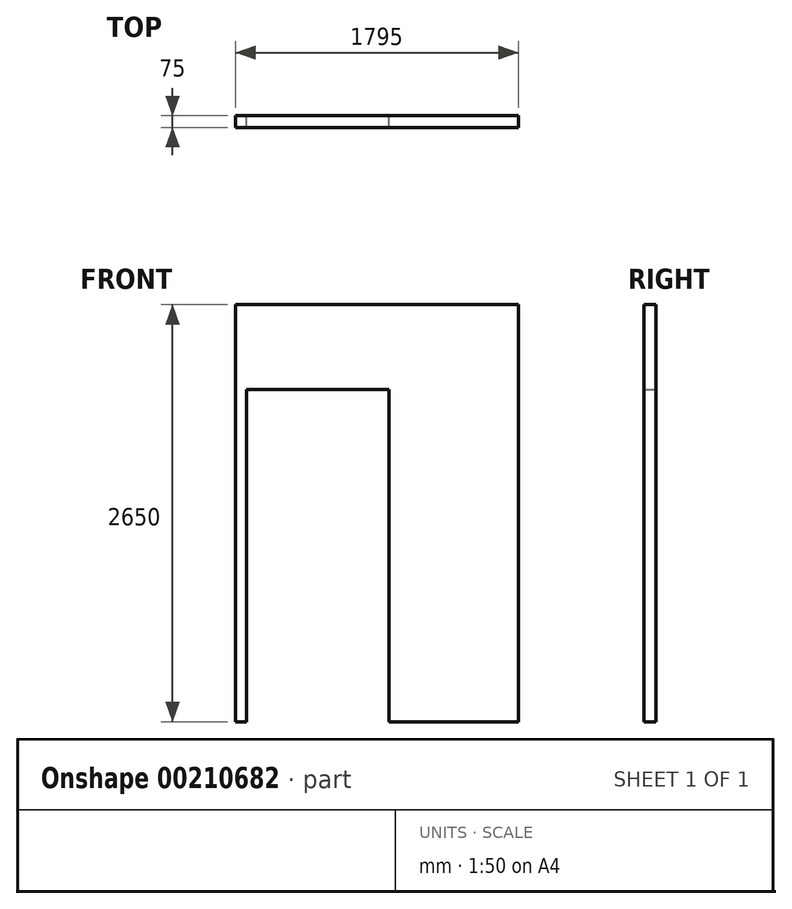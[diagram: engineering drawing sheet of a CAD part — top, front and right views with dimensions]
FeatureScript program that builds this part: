
annotation { "Feature Type Name" : "Feature", "Feature Type Description" : "" }
export const myFeature = defineFeature(function(context is Context, id is Id, definition is map)
    precondition{}
    {
        {
            var Q0;
            Q0=qCreatedBy(makeId("Front.planeOp"),FACE);
            var sketch = newSketch(context, id + "F0", { "sketchPlane" : qUnion([Q0])});
            skLineSegment(sketch, "E0.bottom", {"start": v(0, 0) * mm, "end": v(1795, 0) * mm});
            skLineSegment(sketch, "E0.left", {"start": v(0, 0) * mm, "end": v(0, 2650) * mm});
            skLineSegment(sketch, "E0.right", {"start": v(1795, 0) * mm, "end": v(1795, 2650) * mm});
            skLineSegment(sketch, "E1", {"start": v(0, 2650) * mm, "end": v(1795, 2650) * mm});
            skLineSegment(sketch, "E2.bottom", {"start": v(70, 0) * mm, "end": v(975, 0) * mm});
            skLineSegment(sketch, "E2.top", {"start": v(70, 2110) * mm, "end": v(975, 2110) * mm});
            skLineSegment(sketch, "E2.left", {"start": v(70, 0) * mm, "end": v(70, 2110) * mm});
            skLineSegment(sketch, "E2.right", {"start": v(975, 0) * mm, "end": v(975, 2110) * mm});
            skSolve(sketch);
        }
        {
            var Q0;
            Q0=makeQuery(id+"F0.imprint","IMPRINT",FACE,{"disambiguationData":[TD([[makeQuery(id+"F0.imprint","IMPRINT",EDGE,{"derivedFrom":sQuery(id+"F0.wireOp",EDGE,"E0.bottom")}),1.0]])]});
            extrude(context, id + "F1", {"entities" : qUnion([Q0]), "depth" : 75 * mm});
        }
    });
